# Revit family: Faucet-Lavatory-Grohe-Bauloop-23084001
name_source: partatom
category: Plumbing Fixtures
revit_build: Autodesk Revit 2018 (Build: 20170223_1515(x64)
units: mm (PartAtom-declared; Revit-internal decimal feet)

## family parameters
Always vertical = No
Cut with Voids When Loaded = No
OmniClass Number = 23.45.55.14
OmniClass Title = Single Faucets
Part Type = Normal
Room Calculation Point = No
Round Connector Dimension = Use Diameter
Shared = Yes
Work Plane-Based = Yes

## types (1)
- 23084001
    ADA Compliant = Yes
    Assembly Code = D2020300
    CW Connection = Yes
    CWFU = 1.5
    Cold Water Connection Diameter = 1/2"
    Cold Water Connection Radius = 1/4"
    Default Elevation = 0"
    Description = Single Hole Single-Handle S-Size Bathroom Faucet 1.2 GPM
    Finish = Metal-Grohe-001-StarLight Chrome
    Flow Rate = 1.2 GPM
    HW Connection = Yes
    HWFU = 1.5
    Height = 5 13/16"
    Hot Water Connection Diameter = 1"
    Hot Water Connection Radius = 1/4"
    Manufacturer = Grohe
    Material = Metal-Grohe-001-StarLight Chrome
    Model = 23084001
    Price = Prices may vary. Please consult Manufacturer Representative for most up-to-date price list.
    Product Documentation Link = https://americanstandard.box.com
    Product Page URL = https://www.grohe.us
    Revised Date = 04/20/2021
    URL = https://www.grohe.us
    Vent Connection = No
    WFU = 2
    Warranty Information = Limited Lifetime Warranty
    Waste Connection = No
    Width = 1 3/4"

## geometry (parser evidence)
native form markers: Sweep x2
no freeform markers — native parametric forms only
